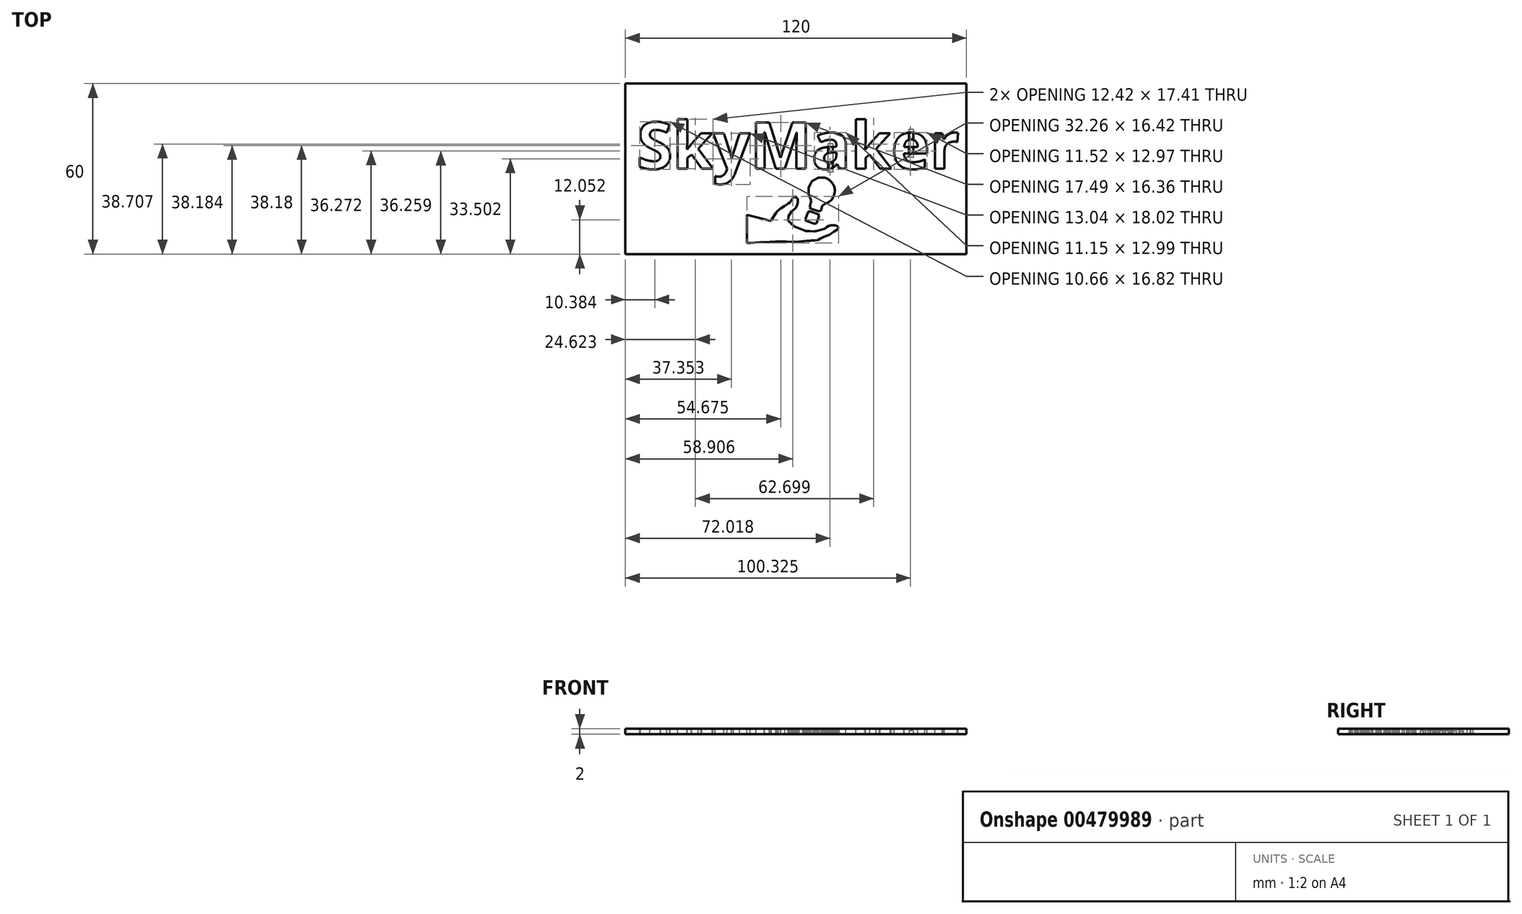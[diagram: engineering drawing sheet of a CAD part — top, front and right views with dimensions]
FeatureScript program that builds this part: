
annotation { "Feature Type Name" : "Feature", "Feature Type Description" : "" }
export const myFeature = defineFeature(function(context is Context, id is Id, definition is map)
    precondition{}
    {
        {
            var Q0;
            Q0=qCreatedBy(makeId("Top.planeOp"),FACE);
            var sketch = newSketch(context, id + "F0", { "sketchPlane" : qUnion([Q0])});
            skLineSegment(sketch, "E0.bottom", {"start": v(-61, 30) * mm, "end": v(59, 30) * mm});
            skLineSegment(sketch, "E0.top", {"start": v(-61, -30) * mm, "end": v(59, -30) * mm});
            skLineSegment(sketch, "E0.left", {"start": v(-61, 30) * mm, "end": v(-61, -30) * mm});
            skLineSegment(sketch, "E0.right", {"start": v(59, 30) * mm, "end": v(59, -30) * mm});
            skSolve(sketch);
        }
        {
            var Q0;
            Q0=qSketchRegion(id+"F0",true);
            extrude(context, id + "F1", {"entities" : qUnion([Q0]), "depth" : 2 * mm});
        }
        {
            var Q0;
            Q0=makeQuery(id+"F1.opExtrude","CAP_FACE",FACE,{"disambiguationData":[OSD([sQuery(id+"F0.wireOp",EDGE,"E0.bottom"),sQuery(id+"F0.wireOp",EDGE,"E0.top"),sQuery(id+"F0.wireOp",EDGE,"E0.left"),sQuery(id+"F0.wireOp",EDGE,"E0.right")])],"isStart":false});
            var sketch = newSketch(context, id + "F2", { "sketchPlane" : qUnion([Q0])});
            skText(sketch, "E1", { "text": "SkyMaker", "fontName": "OpenSans-Bold.ttf"});
            const initialGuessF2  = {"E1": [-0.057, 0, 1, 0, 0.0165]};
            skSetInitialGuess(sketch, initialGuessF2);
            skSolve(sketch);
        }
        {
            var Q0;
            Q0=qSketchRegion(id+"F2",true);
            extrude(context, id + "F3", {"entities" : qUnion([Q0]), "operationType" : NewBodyOperationType.REMOVE, "oppositeDirection" : true, "depth" : 25 * mm});
        }
        {
            var Q0;
            {var subQ0=sQuery(id+"F0.wireOp",EDGE,"E0.top");var subQ1=sQuery(id+"F0.wireOp",EDGE,"E0.right");var subQ2=sQuery(id+"F0.wireOp",EDGE,"E0.bottom");var subQ3=sQuery(id+"F0.wireOp",EDGE,"E0.left");Q0=makeQuery(id+"F3.boolean.opBoolean","SPLIT",FACE,{"disambiguationData":[TD([makeQuery(id+"F1.opExtrude","SWEPT_FACE",FACE,{"disambiguationData":[OSD([subQ2])]})])],"derivedFrom":makeQuery(id+"F1.opExtrude","CAP_FACE",FACE,{"disambiguationData":[OSD([subQ2,subQ0,subQ3,subQ1])],"isStart":false})});}
            var sketch = newSketch(context, id + "F4", { "sketchPlane" : qUnion([Q0])});
            skLineSegment(sketch, "E2", {"start": v(-18.23, -16.16) * mm, "end": v(-18.23, -26.16) * mm});
            skLineSegment(sketch, "E3", {"start": v(-18.23, -26.16) * mm, "end": v(-16.9, -26.06) * mm});
            skLineSegment(sketch, "E4", {"start": v(-16.9, -26.06) * mm, "end": v(-13.82, -25.86) * mm});
            skLineSegment(sketch, "E5", {"start": v(-13.82, -25.86) * mm, "end": v(-10.25, -25.67) * mm});
            skLineSegment(sketch, "E6", {"start": v(-10.25, -25.67) * mm, "end": v(-8.14, -25.58) * mm});
            skLineSegment(sketch, "E7", {"start": v(-8.14, -25.58) * mm, "end": v(-7.5, -25.59) * mm});
            skLineSegment(sketch, "E8", {"start": v(-7.5, -25.59) * mm, "end": v(-7.17, -25.59) * mm});
            skLineSegment(sketch, "E9", {"start": v(-7.17, -25.59) * mm, "end": v(-6.14, -25.6) * mm});
            skLineSegment(sketch, "E10", {"start": v(-6.14, -25.6) * mm, "end": v(-4.27, -25.64) * mm});
            skLineSegment(sketch, "E11", {"start": v(-4.27, -25.64) * mm, "end": v(-2.49, -25.67) * mm});
            skLineSegment(sketch, "E12", {"start": v(-2.49, -25.67) * mm, "end": v(-1.59, -25.68) * mm});
            skLineSegment(sketch, "E13", {"start": v(-1.59, -25.68) * mm, "end": v(-1.41, -25.68) * mm});
            skLineSegment(sketch, "E14", {"start": v(-1.41, -25.68) * mm, "end": v(-1.21, -25.67) * mm});
            skLineSegment(sketch, "E15", {"start": v(-1.21, -25.67) * mm, "end": v(0.11, -25.57) * mm});
            skLineSegment(sketch, "E16", {"start": v(0.11, -25.57) * mm, "end": v(1.43, -25.45) * mm});
            skLineSegment(sketch, "E17", {"start": v(1.43, -25.45) * mm, "end": v(1.62, -25.44) * mm});
            skLineSegment(sketch, "E18", {"start": v(1.62, -25.44) * mm, "end": v(1.8, -25.42) * mm});
            skLineSegment(sketch, "E19", {"start": v(1.8, -25.42) * mm, "end": v(2.72, -25.38) * mm});
            skLineSegment(sketch, "E20", {"start": v(2.72, -25.38) * mm, "end": v(3.75, -25.32) * mm});
            skLineSegment(sketch, "E21", {"start": v(3.75, -25.32) * mm, "end": v(4, -25.3) * mm});
            skLineSegment(sketch, "E22", {"start": v(4, -25.3) * mm, "end": v(4.33, -25.27) * mm});
            skLineSegment(sketch, "E23", {"start": v(4.33, -25.27) * mm, "end": v(5.62, -25.22) * mm});
            skLineSegment(sketch, "E24", {"start": v(5.62, -25.22) * mm, "end": v(6.62, -25.06) * mm});
            skLineSegment(sketch, "E25", {"start": v(6.62, -25.06) * mm, "end": v(6.8, -24.98) * mm});
            skLineSegment(sketch, "E26", {"start": v(6.8, -24.98) * mm, "end": v(6.93, -24.93) * mm});
            skLineSegment(sketch, "E27", {"start": v(6.93, -24.93) * mm, "end": v(7.57, -24.58) * mm});
            skLineSegment(sketch, "E28", {"start": v(7.57, -24.58) * mm, "end": v(8.35, -24.16) * mm});
            skLineSegment(sketch, "E29", {"start": v(8.35, -24.16) * mm, "end": v(8.54, -24.07) * mm});
            skLineSegment(sketch, "E30", {"start": v(8.54, -24.07) * mm, "end": v(8.81, -23.95) * mm});
            skLineSegment(sketch, "E31", {"start": v(8.81, -23.95) * mm, "end": v(9.87, -23.55) * mm});
            skLineSegment(sketch, "E32", {"start": v(9.87, -23.55) * mm, "end": v(10.6, -23.3) * mm});
            skLineSegment(sketch, "E33", {"start": v(10.6, -23.3) * mm, "end": v(10.7, -23.25) * mm});
            skLineSegment(sketch, "E34", {"start": v(10.7, -23.25) * mm, "end": v(10.8, -23.2) * mm});
            skLineSegment(sketch, "E35", {"start": v(10.8, -23.2) * mm, "end": v(11.37, -22.8) * mm});
            skLineSegment(sketch, "E36", {"start": v(11.37, -22.8) * mm, "end": v(12.1, -22.24) * mm});
            skLineSegment(sketch, "E37", {"start": v(12.1, -22.24) * mm, "end": v(12.29, -22.11) * mm});
            skLineSegment(sketch, "E38", {"start": v(12.29, -22.11) * mm, "end": v(12.47, -22) * mm});
            skLineSegment(sketch, "E39", {"start": v(12.47, -22) * mm, "end": v(13.47, -21.4) * mm});
            skLineSegment(sketch, "E40", {"start": v(13.47, -21.4) * mm, "end": v(14.04, -20.92) * mm});
            skLineSegment(sketch, "E41", {"start": v(14.04, -20.92) * mm, "end": v(14.02, -20.85) * mm});
            skLineSegment(sketch, "E42", {"start": v(14.02, -20.85) * mm, "end": v(13.95, -20.67) * mm});
            skLineSegment(sketch, "E43", {"start": v(13.95, -20.67) * mm, "end": v(13.54, -20.19) * mm});
            skLineSegment(sketch, "E44", {"start": v(13.54, -20.19) * mm, "end": v(12.8, -19.88) * mm});
            skLineSegment(sketch, "E45", {"start": v(12.8, -19.88) * mm, "end": v(11.91, -19.84) * mm});
            skLineSegment(sketch, "E46", {"start": v(11.91, -19.84) * mm, "end": v(11.22, -19.92) * mm});
            skLineSegment(sketch, "E47", {"start": v(11.22, -19.92) * mm, "end": v(11, -19.97) * mm});
            skLineSegment(sketch, "E48", {"start": v(11, -19.97) * mm, "end": v(10.85, -20) * mm});
            skLineSegment(sketch, "E49", {"start": v(10.85, -20) * mm, "end": v(10.45, -20.2) * mm});
            skLineSegment(sketch, "E50", {"start": v(10.45, -20.2) * mm, "end": v(9.88, -20.57) * mm});
            skLineSegment(sketch, "E51", {"start": v(9.88, -20.57) * mm, "end": v(9.42, -20.92) * mm});
            skLineSegment(sketch, "E52", {"start": v(9.42, -20.92) * mm, "end": v(9.24, -21.08) * mm});
            skLineSegment(sketch, "E53", {"start": v(9.24, -21.08) * mm, "end": v(8.96, -21.13) * mm});
            skLineSegment(sketch, "E54", {"start": v(8.96, -21.13) * mm, "end": v(6.17, -21.86) * mm});
            skLineSegment(sketch, "E55", {"start": v(6.17, -21.86) * mm, "end": v(5.9, -21.95) * mm});
            skLineSegment(sketch, "E56", {"start": v(5.9, -21.95) * mm, "end": v(5.54, -21.98) * mm});
            skLineSegment(sketch, "E57", {"start": v(5.54, -21.98) * mm, "end": v(3.92, -21.94) * mm});
            skLineSegment(sketch, "E58", {"start": v(3.92, -21.94) * mm, "end": v(2.7, -21.89) * mm});
            skLineSegment(sketch, "E59", {"start": v(2.7, -21.89) * mm, "end": v(2.56, -21.9) * mm});
            skLineSegment(sketch, "E60", {"start": v(2.56, -21.9) * mm, "end": v(2.25, -21.76) * mm});
            skLineSegment(sketch, "E61", {"start": v(2.25, -21.76) * mm, "end": v(-0.95, -20.58) * mm});
            skLineSegment(sketch, "E62", {"start": v(-0.95, -20.58) * mm, "end": v(-1.28, -20.5) * mm});
            skLineSegment(sketch, "E63", {"start": v(-1.28, -20.5) * mm, "end": v(-1.4, -20.42) * mm});
            skLineSegment(sketch, "E64", {"start": v(-1.4, -20.42) * mm, "end": v(-2.48, -19.45) * mm});
            skLineSegment(sketch, "E65", {"start": v(-2.48, -19.45) * mm, "end": v(-2.57, -19.34) * mm});
            skLineSegment(sketch, "E66", {"start": v(-2.57, -19.34) * mm, "end": v(-2.65, -19.24) * mm});
            skLineSegment(sketch, "E67", {"start": v(-2.65, -19.24) * mm, "end": v(-3.65, -18.36) * mm});
            skLineSegment(sketch, "E68", {"start": v(-3.65, -18.36) * mm, "end": v(-3.77, -18.3) * mm});
            skLineSegment(sketch, "E69", {"start": v(-3.77, -18.3) * mm, "end": v(-3.67, -16.67) * mm});
            skLineSegment(sketch, "E70", {"start": v(-3.67, -16.67) * mm, "end": v(-2.44, -14.9) * mm});
            skLineSegment(sketch, "E71", {"start": v(-2.44, -14.9) * mm, "end": v(-2.3, -14.82) * mm});
            skLineSegment(sketch, "E72", {"start": v(-2.3, -14.82) * mm, "end": v(-1.11, -13.77) * mm});
            skLineSegment(sketch, "E73", {"start": v(-1.11, -13.77) * mm, "end": v(-1.01, -13.65) * mm});
            skLineSegment(sketch, "E74", {"start": v(-1.01, -13.65) * mm, "end": v(-0.9, -13.45) * mm});
            skLineSegment(sketch, "E75", {"start": v(-0.9, -13.45) * mm, "end": v(-0.6, -12.8) * mm});
            skLineSegment(sketch, "E76", {"start": v(-0.6, -12.8) * mm, "end": v(-0.31, -11.83) * mm});
            skLineSegment(sketch, "E77", {"start": v(-0.31, -11.83) * mm, "end": v(-0.3, -10.91) * mm});
            skLineSegment(sketch, "E78", {"start": v(-0.3, -10.91) * mm, "end": v(-0.53, -10.33) * mm});
            skLineSegment(sketch, "E79", {"start": v(-0.53, -10.33) * mm, "end": v(-0.67, -10.21) * mm});
            skLineSegment(sketch, "E80", {"start": v(-0.67, -10.21) * mm, "end": v(-0.85, -10.05) * mm});
            skLineSegment(sketch, "E81", {"start": v(-0.85, -10.05) * mm, "end": v(-1.54, -9.74) * mm});
            skLineSegment(sketch, "E82", {"start": v(-1.54, -9.74) * mm, "end": v(-1.8, -9.8) * mm});
            skLineSegment(sketch, "E83", {"start": v(-1.8, -9.8) * mm, "end": v(-1.89, -9.97) * mm});
            skLineSegment(sketch, "E84", {"start": v(-1.89, -9.97) * mm, "end": v(-2.9, -11.55) * mm});
            skLineSegment(sketch, "E85", {"start": v(-2.9, -11.55) * mm, "end": v(-3.03, -11.7) * mm});
            skLineSegment(sketch, "E86", {"start": v(-3.03, -11.7) * mm, "end": v(-3.2, -11.88) * mm});
            skLineSegment(sketch, "E87", {"start": v(-3.2, -11.88) * mm, "end": v(-3.81, -12.32) * mm});
            skLineSegment(sketch, "E88", {"start": v(-3.81, -12.32) * mm, "end": v(-4.97, -13.04) * mm});
            skLineSegment(sketch, "E89", {"start": v(-4.97, -13.04) * mm, "end": v(-6.34, -13.97) * mm});
            skLineSegment(sketch, "E90", {"start": v(-6.34, -13.97) * mm, "end": v(-7.43, -14.86) * mm});
            skLineSegment(sketch, "E91", {"start": v(-7.43, -14.86) * mm, "end": v(-7.76, -15.2) * mm});
            skLineSegment(sketch, "E92", {"start": v(-7.76, -15.2) * mm, "end": v(-7.97, -15.42) * mm});
            skLineSegment(sketch, "E93", {"start": v(-7.97, -15.42) * mm, "end": v(-9.6, -18.01) * mm});
            skLineSegment(sketch, "E94", {"start": v(-9.6, -18.01) * mm, "end": v(-9.72, -18.3) * mm});
            skLineSegment(sketch, "E95", {"start": v(-9.72, -18.3) * mm, "end": v(-18.23, -16.16) * mm});
            skLineSegment(sketch, "E96", {"start": v(7.1, -16.52) * mm, "end": v(6.24, -19.06) * mm});
            skLineSegment(sketch, "E97", {"start": v(6.24, -19.06) * mm, "end": v(5.63, -19.34) * mm});
            skLineSegment(sketch, "E98", {"start": v(5.63, -19.34) * mm, "end": v(2.75, -18.35) * mm});
            skLineSegment(sketch, "E99", {"start": v(2.75, -18.35) * mm, "end": v(2.34, -17.78) * mm});
            skLineSegment(sketch, "E100", {"start": v(2.34, -17.78) * mm, "end": v(3.2, -15.25) * mm});
            skLineSegment(sketch, "E101", {"start": v(3.2, -15.25) * mm, "end": v(3.85, -14.93) * mm});
            skLineSegment(sketch, "E102", {"start": v(3.85, -14.93) * mm, "end": v(6.76, -15.93) * mm});
            skLineSegment(sketch, "E103", {"start": v(6.76, -15.93) * mm, "end": v(7.1, -16.52) * mm});
            skLineSegment(sketch, "E104", {"start": v(10.54, -11.68) * mm, "end": v(10.81, -11.5) * mm});
            skLineSegment(sketch, "E105", {"start": v(10.81, -11.5) * mm, "end": v(11.54, -10.82) * mm});
            skLineSegment(sketch, "E106", {"start": v(11.54, -10.82) * mm, "end": v(12.25, -9.73) * mm});
            skLineSegment(sketch, "E107", {"start": v(12.25, -9.73) * mm, "end": v(12.64, -8.49) * mm});
            skLineSegment(sketch, "E108", {"start": v(12.64, -8.49) * mm, "end": v(12.7, -7.49) * mm});
            skLineSegment(sketch, "E109", {"start": v(12.7, -7.49) * mm, "end": v(12.67, -7.16) * mm});
            skLineSegment(sketch, "E110", {"start": v(12.67, -7.16) * mm, "end": v(12.63, -6.84) * mm});
            skLineSegment(sketch, "E111", {"start": v(12.63, -6.84) * mm, "end": v(12.32, -5.88) * mm});
            skLineSegment(sketch, "E112", {"start": v(12.32, -5.88) * mm, "end": v(11.65, -4.77) * mm});
            skLineSegment(sketch, "E113", {"start": v(11.65, -4.77) * mm, "end": v(10.7, -3.88) * mm});
            skLineSegment(sketch, "E114", {"start": v(10.7, -3.88) * mm, "end": v(9.83, -3.4) * mm});
            skLineSegment(sketch, "E115", {"start": v(9.83, -3.4) * mm, "end": v(9.52, -3.29) * mm});
            skLineSegment(sketch, "E116", {"start": v(9.52, -3.29) * mm, "end": v(9.1, -3.14) * mm});
            skLineSegment(sketch, "E117", {"start": v(9.1, -3.14) * mm, "end": v(6.93, -3.16) * mm});
            skLineSegment(sketch, "E118", {"start": v(6.93, -3.16) * mm, "end": v(4.98, -4.1) * mm});
            skLineSegment(sketch, "E119", {"start": v(4.98, -4.1) * mm, "end": v(4.66, -4.43) * mm});
            skLineSegment(sketch, "E120", {"start": v(4.66, -4.43) * mm, "end": v(4.35, -4.75) * mm});
            skLineSegment(sketch, "E121", {"start": v(4.35, -4.75) * mm, "end": v(3.42, -6.71) * mm});
            skLineSegment(sketch, "E122", {"start": v(3.42, -6.71) * mm, "end": v(3.43, -8.88) * mm});
            skLineSegment(sketch, "E123", {"start": v(3.43, -8.88) * mm, "end": v(3.58, -9.3) * mm});
            skLineSegment(sketch, "E124", {"start": v(3.58, -9.3) * mm, "end": v(3.64, -9.48) * mm});
            skLineSegment(sketch, "E125", {"start": v(3.64, -9.48) * mm, "end": v(3.72, -9.7) * mm});
            skLineSegment(sketch, "E126", {"start": v(3.72, -9.7) * mm, "end": v(4.2, -10.71) * mm});
            skLineSegment(sketch, "E127", {"start": v(4.2, -10.71) * mm, "end": v(4.36, -11.72) * mm});
            skLineSegment(sketch, "E128", {"start": v(4.36, -11.72) * mm, "end": v(4.28, -11.93) * mm});
            skLineSegment(sketch, "E129", {"start": v(4.28, -11.93) * mm, "end": v(3.8, -13.4) * mm});
            skLineSegment(sketch, "E130", {"start": v(3.8, -13.4) * mm, "end": v(4.2, -13.98) * mm});
            skLineSegment(sketch, "E131", {"start": v(4.2, -13.98) * mm, "end": v(7.01, -14.96) * mm});
            skLineSegment(sketch, "E132", {"start": v(7.01, -14.96) * mm, "end": v(7.73, -14.77) * mm});
            skLineSegment(sketch, "E133", {"start": v(7.73, -14.77) * mm, "end": v(8.22, -13.27) * mm});
            skLineSegment(sketch, "E134", {"start": v(8.22, -13.27) * mm, "end": v(8.29, -13.05) * mm});
            skLineSegment(sketch, "E135", {"start": v(8.29, -13.05) * mm, "end": v(9.09, -12.39) * mm});
            skLineSegment(sketch, "E136", {"start": v(9.09, -12.39) * mm, "end": v(10.18, -11.88) * mm});
            skLineSegment(sketch, "E137", {"start": v(10.18, -11.88) * mm, "end": v(10.4, -11.75) * mm});
            skLineSegment(sketch, "E138", {"start": v(10.4, -11.75) * mm, "end": v(10.54, -11.68) * mm});
            skSolve(sketch);
        }
        {
            var Q0;
            Q0=qSketchRegion(id+"F4",true);
            extrude(context, id + "F5", {"entities" : qUnion([Q0]), "operationType" : NewBodyOperationType.REMOVE, "oppositeDirection" : true, "depth" : 25 * mm});
        }
        {
            var Q0;
            {var subQ0=sQuery(id+"F0.wireOp",EDGE,"E0.top");var subQ1=sQuery(id+"F0.wireOp",EDGE,"E0.right");var subQ2=sQuery(id+"F0.wireOp",EDGE,"E0.bottom");var subQ3=sQuery(id+"F0.wireOp",EDGE,"E0.left");Q0=makeQuery(id+"F3.boolean.opBoolean","SPLIT",FACE,{"disambiguationData":[TD([makeQuery(id+"F1.opExtrude","SWEPT_FACE",FACE,{"disambiguationData":[OSD([subQ2])]})])],"derivedFrom":makeQuery(id+"F1.opExtrude","CAP_FACE",FACE,{"disambiguationData":[OSD([subQ2,subQ0,subQ3,subQ1])],"isStart":true})});}
            var sketch = newSketch(context, id + "F6", { "sketchPlane" : qUnion([Q0])});
            skLineSegment(sketch, "E139.bottom", {"start": v(40.34, -13.95) * mm, "end": v(38.74, -13.95) * mm});
            skLineSegment(sketch, "E139.top", {"start": v(40.34, -3.95) * mm, "end": v(38.74, -3.95) * mm});
            skLineSegment(sketch, "E139.left", {"start": v(40.34, -13.95) * mm, "end": v(40.34, -3.95) * mm});
            skLineSegment(sketch, "E140", {"start": v(38.74, -3.95) * mm, "end": v(38.74, -13.95) * mm});
            skLineSegment(sketch, "E141.bottom", {"start": v(11.98, -8.78) * mm, "end": v(10.38, -8.78) * mm});
            skLineSegment(sketch, "E141.top", {"start": v(11.98, 1.22) * mm, "end": v(10.38, 1.22) * mm});
            skLineSegment(sketch, "E141.left", {"start": v(11.98, -8.78) * mm, "end": v(11.98, 1.22) * mm});
            skLineSegment(sketch, "E142", {"start": v(10.38, 1.22) * mm, "end": v(10.38, -8.78) * mm});
            skSolve(sketch);
        }
        {
            var Q0;
            Q0=qSketchRegion(id+"F6",true);
            extrude(context, id + "F7", {"entities" : qUnion([Q0]), "oppositeDirection" : true, "depth" : 1.2 * mm});
        }
    });
